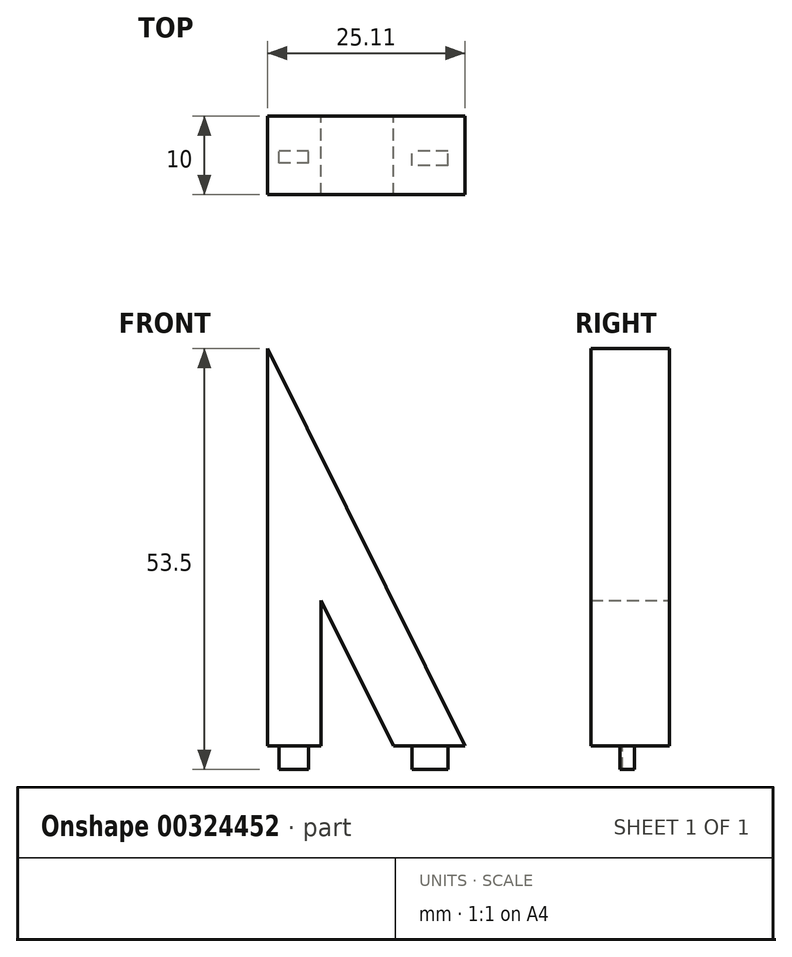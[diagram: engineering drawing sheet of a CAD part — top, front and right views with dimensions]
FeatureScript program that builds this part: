
annotation { "Feature Type Name" : "Feature", "Feature Type Description" : "" }
export const myFeature = defineFeature(function(context is Context, id is Id, definition is map)
    precondition{}
    {
        {
            var Q0;
            Q0=qCreatedBy(makeId("Front.planeOp"),FACE);
            var sketch = newSketch(context, id + "F0", { "sketchPlane" : qUnion([Q0])});
            skLineSegment(sketch, "E0", {"start": v(0, 0) * mm, "end": v(0, 50.5) * mm});
            skLineSegment(sketch, "E1", {"start": v(0, 50.5) * mm, "end": v(25.11, 0) * mm});
            skLineSegment(sketch, "E2", {"start": v(25.11, 0) * mm, "end": v(16.01, 0) * mm});
            skLineSegment(sketch, "E3", {"start": v(16.01, 0) * mm, "end": v(6.84, 18.45) * mm});
            skLineSegment(sketch, "E4", {"start": v(6.84, 18.45) * mm, "end": v(6.84, 0) * mm});
            skLineSegment(sketch, "E5", {"start": v(6.84, 0) * mm, "end": v(0, 0) * mm});
            skSolve(sketch);
        }
        {
            var Q0;
            Q0 = qSketchRegion(id + "F0", true);
            extrude(context, id + "F1", {"entities" : qUnion([Q0]), "depth" : 10 * mm});
        }
        {
            var Q0;
            Q0=makeQuery(id+"F1.opExtrude","SWEPT_FACE",FACE,{"disambiguationData":[OSD([sQuery(id+"F0.wireOp",EDGE,"E5")])]});
            var sketch = newSketch(context, id + "F2", { "sketchPlane" : qUnion([Q0])});
            skLineSegment(sketch, "E6.bottom", {"start": v(5.26, 5.98) * mm, "end": v(1.5, 5.98) * mm});
            skLineSegment(sketch, "E6.top", {"start": v(5.26, 4.48) * mm, "end": v(1.5, 4.48) * mm});
            skLineSegment(sketch, "E6.left", {"start": v(5.26, 5.98) * mm, "end": v(5.26, 4.48) * mm});
            skLineSegment(sketch, "E6.right", {"start": v(1.5, 5.98) * mm, "end": v(1.5, 4.48) * mm});
            skPoint(sketch, "E6.middle", {"position": v(3.38, 5.23) * mm});
            skSolve(sketch);
        }
        {
            var Q0;
            Q0 = qSketchRegion(id + "F2", true);
            extrude(context, id + "F3", {"entities" : qUnion([Q0]), "operationType" : NewBodyOperationType.ADD, "depth" : 3 * mm});
        }
        {
            var Q0;
            Q0=makeQuery(id+"F1.opExtrude","SWEPT_FACE",FACE,{"disambiguationData":[OSD([sQuery(id+"F0.wireOp",EDGE,"E2")])]});
            var sketch = newSketch(context, id + "F4", { "sketchPlane" : qUnion([Q0])});
            skLineSegment(sketch, "E7.bottom", {"start": v(22.95, 6.29) * mm, "end": v(18.35, 6.29) * mm});
            skLineSegment(sketch, "E7.top", {"start": v(22.95, 4.45) * mm, "end": v(18.35, 4.45) * mm});
            skLineSegment(sketch, "E7.left", {"start": v(22.95, 6.29) * mm, "end": v(22.95, 4.45) * mm});
            skLineSegment(sketch, "E7.right", {"start": v(18.35, 6.29) * mm, "end": v(18.35, 4.45) * mm});
            skPoint(sketch, "E7.middle", {"position": v(20.65, 5.37) * mm});
            skSolve(sketch);
        }
        {
            var Q0;
            Q0 = qSketchRegion(id + "F4", true);
            extrude(context, id + "F5", {"entities" : qUnion([Q0]), "operationType" : NewBodyOperationType.ADD, "depth" : 3 * mm});
        }
    });
